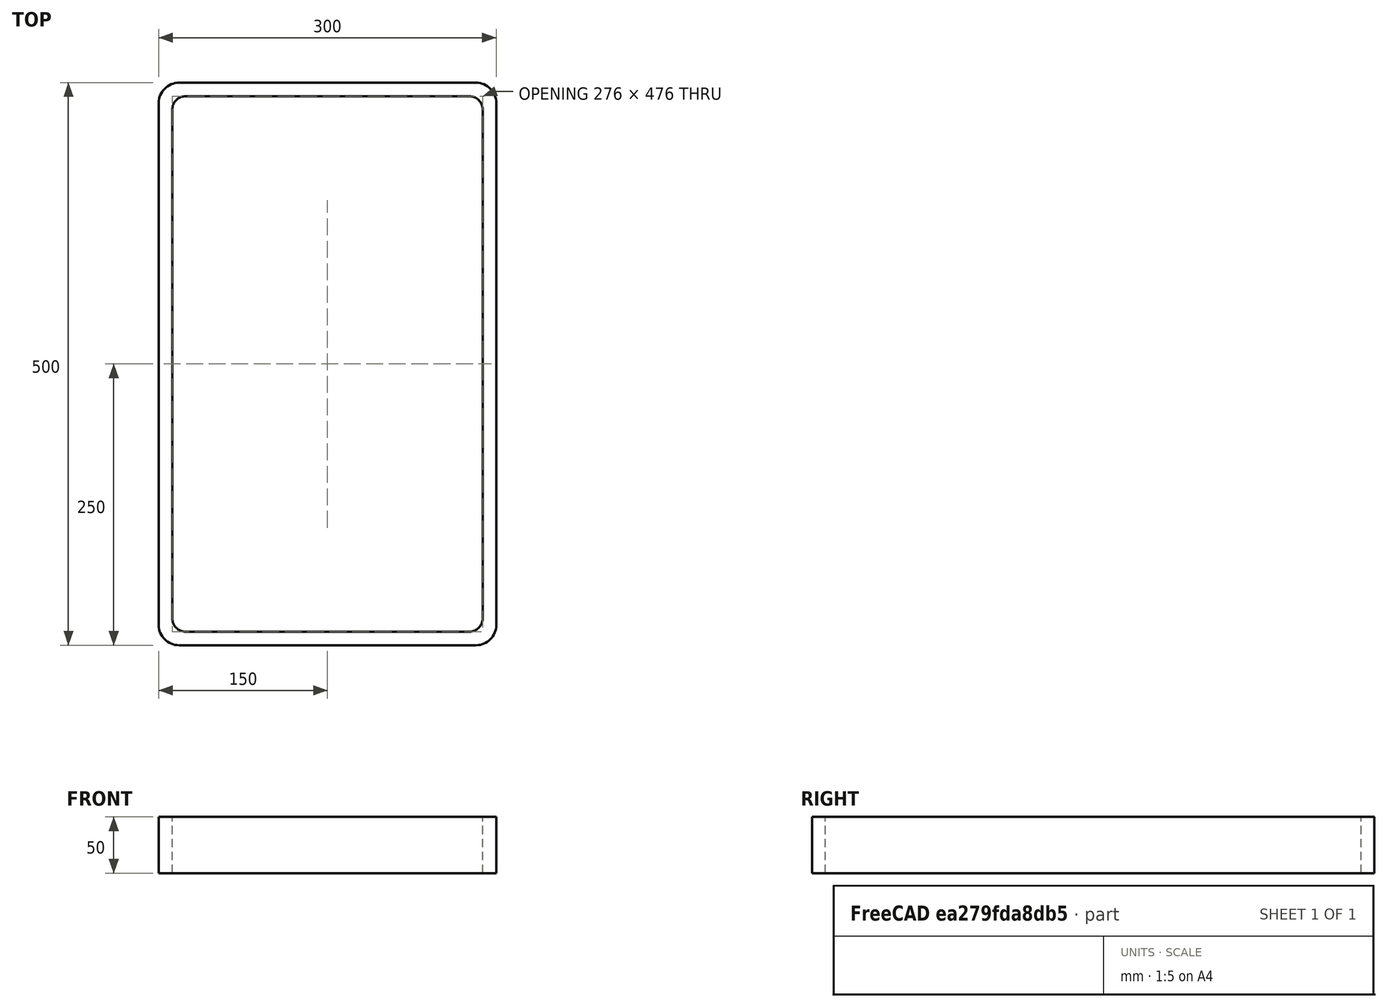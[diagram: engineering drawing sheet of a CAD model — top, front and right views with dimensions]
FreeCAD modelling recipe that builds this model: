
FCSTD DOCUMENT  (FreeCAD 0.15R4671 (Git))
Label: Rectangular hollow section 500x300x12 EN10219 S235JRH
License: All rights reserved
LicenseURL: http://en.wikipedia.org/wiki/All_rights_reserved
objects: Sketcher::SketchObject×1, Part::Extrusion×1
note: 2 computed .brp shape members not serialized (recipe doc carries the construction recipe); baked Part::Feature solids carry a one-line shape summary decoded from their .brp

FEATURE [Sketcher::SketchObject] Sketch
  sketch-geometry (16):
    g0: LineSegment StartX=-126 StartY=238 StartZ=0 EndX=126 EndY=238 EndZ=0
    g1: LineSegment StartX=138 StartY=226 StartZ=0 EndX=138 EndY=-226 EndZ=0
    g2: LineSegment StartX=126 StartY=-238 StartZ=0 EndX=-126 EndY=-238 EndZ=0
    g3: LineSegment StartX=-138 StartY=-226 StartZ=0 EndX=-138 EndY=226 EndZ=0
    g4: LineSegment StartX=-132 StartY=250 StartZ=0 EndX=132 EndY=250 EndZ=0
    g5: LineSegment StartX=150 StartY=232 StartZ=0 EndX=150 EndY=-232 EndZ=0
    g6: LineSegment StartX=132 StartY=-250 StartZ=0 EndX=-132 EndY=-250 EndZ=0
    g7: LineSegment StartX=-150 StartY=-232 StartZ=0 EndX=-150 EndY=232 EndZ=0
    g8: ArcOfCircle CenterX=-126 CenterY=226 CenterZ=0 NormalX=0 NormalY=0 NormalZ=1 Radius=12 StartAngle=1.5708 EndAngle=3.14159
    g9: ArcOfCircle CenterX=126 CenterY=226 CenterZ=0 NormalX=0 NormalY=0 NormalZ=1 Radius=12 StartAngle=0 EndAngle=1.5708
    g10: ArcOfCircle CenterX=126 CenterY=-226 CenterZ=0 NormalX=0 NormalY=0 NormalZ=1 Radius=12 StartAngle=4.71239 EndAngle=6.28319
    g11: ArcOfCircle CenterX=-126 CenterY=-226 CenterZ=0 NormalX=0 NormalY=0 NormalZ=1 Radius=12 StartAngle=3.14159 EndAngle=4.71239
    g12: ArcOfCircle CenterX=132 CenterY=232 CenterZ=0 NormalX=0 NormalY=0 NormalZ=1 Radius=18 StartAngle=0 EndAngle=1.5708
    g13: ArcOfCircle CenterX=132 CenterY=-232 CenterZ=0 NormalX=0 NormalY=0 NormalZ=1 Radius=18 StartAngle=4.71239 EndAngle=6.28319
    g14: ArcOfCircle CenterX=-132 CenterY=-232 CenterZ=0 NormalX=0 NormalY=0 NormalZ=1 Radius=18 StartAngle=3.14159 EndAngle=4.71239
    g15: ArcOfCircle CenterX=-132 CenterY=232 CenterZ=0 NormalX=0 NormalY=0 NormalZ=1 Radius=18 StartAngle=1.5708 EndAngle=3.14159
  constraints (36):
    c: Horizontal(g2)
    c: Vertical(g3)
    c: Horizontal(g6)
    c: Vertical(g7)
    c: Tangent(g3,g8) = 1.5708
    c: Tangent(g0,g8) = 1.5708
    c: Tangent(g0,g9) = 1.5708
    c: Tangent(g1,g9) = 1.5708
    c: Tangent(g1,g10) = 1.5708
    c: Tangent(g2,g10) = 1.5708
    c: Tangent(g2,g11) = 1.5708
    c: Tangent(g3,g11) = 1.5708
    c: Tangent(g4,g12) = 1.5708
    c: Tangent(g5,g12) = 1.5708
    c: Tangent(g5,g13) = 1.5708
    c: Tangent(g6,g13) = 1.5708
    c: Tangent(g6,g14) = 1.5708
    c: Tangent(g7,g14) = 1.5708
    c: Tangent(g7,g15) = 1.5708
    c: Tangent(g4,g15) = 1.5708
    c: Equal(g9,g8)
    c: Equal(g9,g11)
    c: Equal(g9,g10)
    c: Equal(g12,g15)
    c: Equal(g12,g14)
    c: Equal(g12,g13)
    c: Symmetric(g4,g6,g-1)
    c: Symmetric(g7,g5,g-2)
    c: DistanceY(g4,g6) = -500
    c: DistanceX(g7,g5) = 300
    c: Symmetric(g3,g1,g-2)
    c: Symmetric(g0,g2,g-1)
    c: DistanceY(g0,g4) = 12
    c: DistanceX(g5,g1) = -12
    c: Radius(g9) = 12
    c: Radius(g12) = 18
FEATURE [Part::Extrusion] Extrude  label="Rectangular hollow section 500x300x12 EN10219 S235JRH"
  Base = -> Sketch
  Dir = (0,0,50)
  Solid = true
